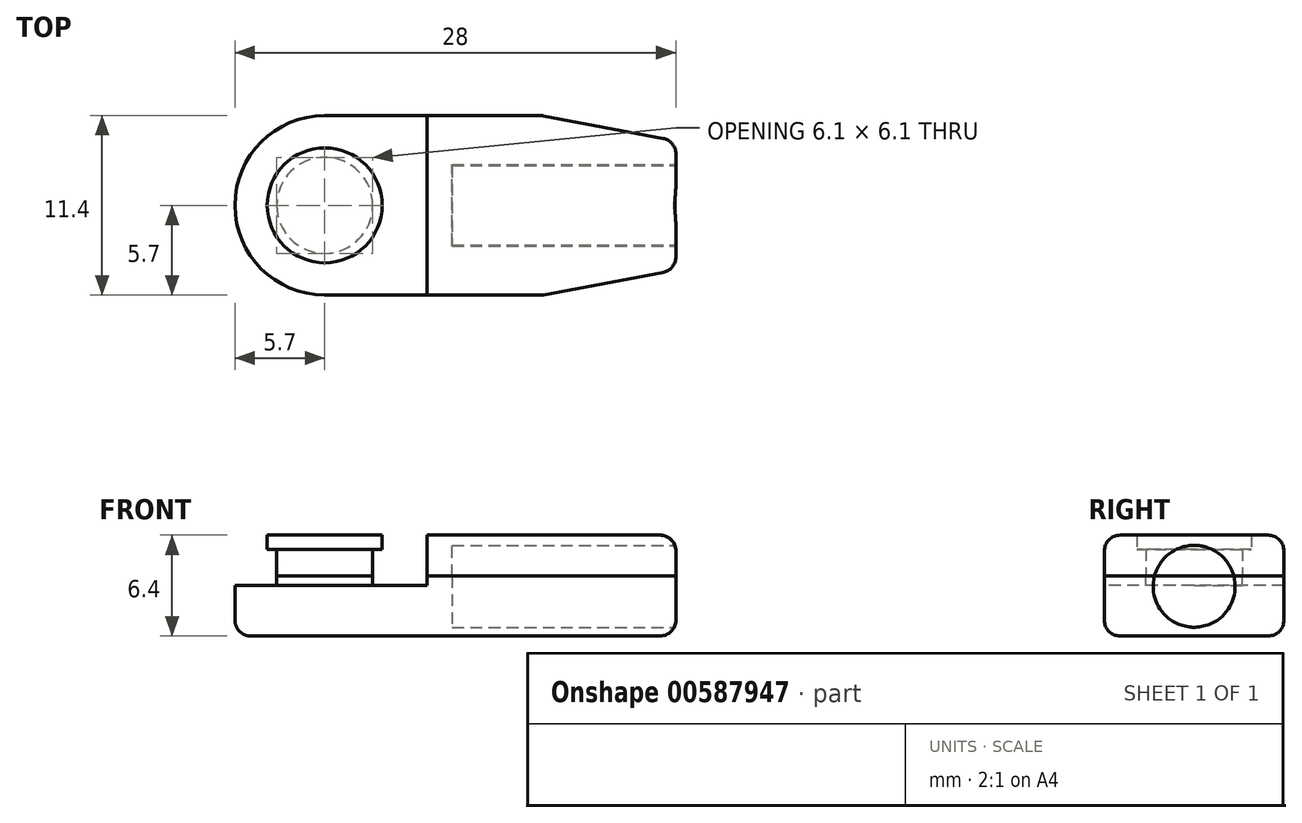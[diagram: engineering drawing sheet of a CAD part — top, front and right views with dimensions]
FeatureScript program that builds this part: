
annotation { "Feature Type Name" : "Feature", "Feature Type Description" : "" }
export const myFeature = defineFeature(function(context is Context, id is Id, definition is map)
    precondition{}
    {
        {
            var Q0;
            Q0=qCreatedBy(makeId("Top.planeOp"),FACE);
            var sketch = newSketch(context, id + "F0", { "sketchPlane" : qUnion([Q0])});
            skLineSegment(sketch, "E0.bottom", {"start": v(6.5, 5.7) * mm, "end": v(13.8, 5.7) * mm});
            skLineSegment(sketch, "E0.top", {"start": v(6.5, -5.7) * mm, "end": v(13.8, -5.7) * mm});
            skLineSegment(sketch, "E0.left", {"start": v(6.5, 5.7) * mm, "end": v(6.5, -5.7) * mm});
            skLineSegment(sketch, "E1", {"start": v(22.3, 4.1) * mm, "end": v(22.3, -4.1) * mm});
            skLineSegment(sketch, "E2", {"start": v(22.3, 4.1) * mm, "end": v(13.8, 5.7) * mm});
            skLineSegment(sketch, "E3", {"start": v(13.8, -5.7) * mm, "end": v(22.3, -4.1) * mm});
            skLineSegment(sketch, "E4.bottom", {"start": v(6.5, 5.7) * mm, "end": v(0, 5.7) * mm});
            skLineSegment(sketch, "E4.top", {"start": v(6.5, -5.7) * mm, "end": v(0, -5.7) * mm});
            skArc(sketch, "E5", {"start": v(0, 5.7) * mm, "mid": v(-5.7, 0) * mm, "end": v(0, -5.7) * mm});
            skCircle(sketch, "E6", {"center": v(0, 0) * mm, "radius": 3.05 * mm});
            skCircle(sketch, "E7", {"center": v(0, 0) * mm, "radius": 3.65 * mm});
            skLineSegment(sketch, "E8", {"start": v(-5.7, 0) * mm, "end": v(22.3, 0) * mm});
            skSolve(sketch);
        }
        {
            var Q0;
            Q0=makeQuery(id+"F0.imprint","IMPRINT",FACE,{"disambiguationData":[TD([[makeQuery(id+"F0.imprint","IMPRINT",EDGE,{"derivedFrom":sQuery(id+"F0.wireOp",EDGE,"E6")}),1.0]])]});
            extrude(context, id + "F1", {"entities" : qUnion([Q0]), "depth" : 1.7 * mm, "offsetDistance" : 25 * mm});
        }
        {
            var Q0;
            Q0=makeQuery(id+"F0.imprint","IMPRINT",FACE,{"disambiguationData":[TD([[makeQuery(id+"F0.imprint","IMPRINT",EDGE,{"derivedFrom":sQuery(id+"F0.wireOp",EDGE,"E0.bottom")}),-1.0]])]});
            var Q1;
            {var subQ1=sQuery(id+"F0.wireOp",EDGE,"E0.top");Q1=makeQuery(id+"F0.imprint","IMPRINT",FACE,{"disambiguationData":[TD([[makeQuery(id+"F0.imprint","IMPRINT",EDGE,{"derivedFrom":subQ1}),1.0]])]});}
            extrude(context, id + "F2", {"entities" : qUnion([Q0, Q1]), "depth" : 2.6 * mm, "offsetDistance" : 25 * mm});
        }
        {
            var Q0;
            Q0=makeQuery(id+"F0.imprint","IMPRINT",FACE,{"disambiguationData":[TD([[makeQuery(id+"F0.imprint","IMPRINT",EDGE,{"derivedFrom":sQuery(id+"F0.wireOp",EDGE,"E4.bottom")}),1.0]])]});
            var Q1;
            Q1=makeQuery(id+"F0.imprint","IMPRINT",FACE,{"disambiguationData":[TD([[makeQuery(id+"F0.imprint","IMPRINT",EDGE,{"derivedFrom":sQuery(id+"F0.wireOp",EDGE,"E0.bottom")}),-1.0]])]});
            var Q2;
            Q2=makeQuery(id+"F0.imprint","IMPRINT",FACE,{"disambiguationData":[TD([[makeQuery(id+"F0.imprint","IMPRINT",EDGE,{"derivedFrom":sQuery(id+"F0.wireOp",EDGE,"E6")}),-1.0]])]});
            var Q3;
            Q3=makeQuery(id+"F0.imprint","IMPRINT",FACE,{"disambiguationData":[TD([[makeQuery(id+"F0.imprint","IMPRINT",EDGE,{"derivedFrom":sQuery(id+"F0.wireOp",EDGE,"E6")}),1.0]])]});
            var Q4;
            {var subQ5=sQuery(id+"F0.wireOp",EDGE,"E4.top");Q4=makeQuery(id+"F0.imprint","IMPRINT",FACE,{"disambiguationData":[TD([[makeQuery(id+"F0.imprint","IMPRINT",EDGE,{"derivedFrom":subQ5}),-1.0]])]});}
            var Q5;
            {var subQ1=sQuery(id+"F0.wireOp",EDGE,"E0.top");Q5=makeQuery(id+"F0.imprint","IMPRINT",FACE,{"disambiguationData":[TD([[makeQuery(id+"F0.imprint","IMPRINT",EDGE,{"derivedFrom":subQ1}),1.0]])]});}
            extrude(context, id + "F3", {"entities" : qUnion([Q0, Q1, Q2, Q3, Q4, Q5]), "depth" : -3.8 * mm, "offsetDistance" : 25 * mm});
        }
        {
            var Q0;
            Q0=makeQuery(id+"F2.opExtrude","SWEPT_FACE",FACE,{"disambiguationData":[OSD([sQuery(id+"F0.wireOp",EDGE,"E1")])]});
            var sketch = newSketch(context, id + "F4", { "sketchPlane" : qUnion([Q0])});
            skCircle(sketch, "E9", {"center": v(0, -0.65) * mm, "radius": 2.6 * mm});
            skSolve(sketch);
        }
        {
            var Q0;
            {var subQ0=sQuery(id+"F4.wireOp",EDGE,"E9");var subQ1=makeQuery(id+"F2.opExtrude","CAP_EDGE",EDGE,{"disambiguationData":[OSD([sQuery(id+"F0.wireOp",EDGE,"E1")])],"isStart":true});var subQ2=makeQuery(id+"F4.imprint","INTERSECT",VERTEX,{"disambiguationData":[OD(0.0)],"derivedFrom":[subQ1,subQ0]});Q0=makeQuery(id+"F4.imprint","IMPRINT",FACE,{"disambiguationData":[TD([[makeQuery(id+"F4.imprint","IMPRINT",EDGE,{"disambiguationData":[TD([[subQ2,-1.0]])],"derivedFrom":subQ0}),1.0]])]});}
            var Q1;
            {var subQ0=sQuery(id+"F4.wireOp",EDGE,"E9");var subQ1=makeQuery(id+"F2.opExtrude","CAP_EDGE",EDGE,{"disambiguationData":[OSD([sQuery(id+"F0.wireOp",EDGE,"E1")])],"isStart":true});var subQ2=makeQuery(id+"F4.imprint","INTERSECT",VERTEX,{"disambiguationData":[OD(0.0)],"derivedFrom":[subQ1,subQ0]});Q1=makeQuery(id+"F4.imprint","IMPRINT",FACE,{"disambiguationData":[TD([[makeQuery(id+"F4.imprint","IMPRINT",EDGE,{"disambiguationData":[TD([[subQ2,1.0]])],"derivedFrom":subQ0}),1.0]])]});}
            var Q2;
            Q2=sQuery(id+"F4.wireOp",EDGE,"E9");
            extrude(context, id + "F5", {"entities" : qUnion([Q0, Q1]), "operationType" : NewBodyOperationType.REMOVE, "surfaceEntities" : qUnion([Q2]), "oppositeDirection" : true, "depth" : 14.2 * mm, "offsetDistance" : 25 * mm});
        }
        {
            var Q0;
            Q0=makeQuery(id+"F1.opExtrude","CAP_FACE",FACE,{"disambiguationData":[OSD([sQuery(id+"F0.wireOp",EDGE,"E6")])],"isStart":false});
            var sketch = newSketch(context, id + "F6", { "sketchPlane" : qUnion([Q0])});
            skCircle(sketch, "E10.0", {"center": v(0, 0) * mm, "radius": 3.65 * mm});
            skSolve(sketch);
        }
        {
            var Q0;
            Q0 = qSketchRegion(id + "F6", true);
            extrude(context, id + "F7", {"entities" : qUnion([Q0]), "operationType" : NewBodyOperationType.ADD, "depth" : 0.9 * mm, "offsetDistance" : 25 * mm});
        }
        {
            var Q0;
            Q0=makeQuery(id+"F0.imprint","IMPRINT",FACE,{"disambiguationData":[TD([[makeQuery(id+"F0.imprint","IMPRINT",EDGE,{"derivedFrom":sQuery(id+"F0.wireOp",EDGE,"E4.bottom")}),1.0]])]});
            var Q1;
            Q1=makeQuery(id+"F0.imprint","IMPRINT",FACE,{"disambiguationData":[TD([[makeQuery(id+"F0.imprint","IMPRINT",EDGE,{"derivedFrom":sQuery(id+"F0.wireOp",EDGE,"E6")}),-1.0]])]});
            var Q2;
            {var subQ5=sQuery(id+"F0.wireOp",EDGE,"E4.top");Q2=makeQuery(id+"F0.imprint","IMPRINT",FACE,{"disambiguationData":[TD([[makeQuery(id+"F0.imprint","IMPRINT",EDGE,{"derivedFrom":subQ5}),-1.0]])]});}
            extrude(context, id + "F8", {"entities" : qUnion([Q0, Q1, Q2]), "operationType" : NewBodyOperationType.REMOVE, "oppositeDirection" : true, "depth" : 0.6 * mm, "offsetDistance" : 25 * mm});
        }
        {
            var Q0;
            Q0=makeQuery(id+"F2.opExtrude","CAP_EDGE",EDGE,{"disambiguationData":[OSD([sQuery(id+"F0.wireOp",EDGE,"E0.top")])],"isStart":false});
            var Q1;
            Q1=makeQuery(id+"F2.opExtrude","CAP_EDGE",EDGE,{"disambiguationData":[OSD([sQuery(id+"F0.wireOp",EDGE,"E3")])],"isStart":false});
            var Q2;
            Q2=makeQuery(id+"F2.opExtrude","CAP_EDGE",EDGE,{"disambiguationData":[OSD([sQuery(id+"F0.wireOp",EDGE,"E1")])],"isStart":false});
            var Q3;
            Q3=makeQuery(id+"F2.opExtrude","CAP_EDGE",EDGE,{"disambiguationData":[OSD([sQuery(id+"F0.wireOp",EDGE,"E2")])],"isStart":false});
            var Q4;
            Q4=makeQuery(id+"F2.opExtrude","CAP_EDGE",EDGE,{"disambiguationData":[OSD([sQuery(id+"F0.wireOp",EDGE,"E0.bottom")])],"isStart":false});
            var Q5;
            Q5=makeQuery(id+"F3.opExtrude","CAP_EDGE",EDGE,{"disambiguationData":[OSD([sQuery(id+"F0.wireOp",EDGE,"E1")])],"isStart":false});
            var Q6;
            Q6=makeQuery(id+"F3.opExtrude","SWEPT_EDGE",EDGE,{"disambiguationData":[OSD([sQuery(id+"F0.wireOp",EDGE,"E1"),sQuery(id+"F0.wireOp",EDGE,"E2")])]});
            var Q7;
            Q7=makeQuery(id+"F2.opExtrude","SWEPT_EDGE",EDGE,{"disambiguationData":[OSD([sQuery(id+"F0.wireOp",EDGE,"E1"),sQuery(id+"F0.wireOp",EDGE,"E2")])]});
            var Q8;
            Q8=makeQuery(id+"F3.opExtrude","SWEPT_EDGE",EDGE,{"disambiguationData":[OSD([sQuery(id+"F0.wireOp",EDGE,"E1"),sQuery(id+"F0.wireOp",EDGE,"E3")])]});
            var Q9;
            Q9=makeQuery(id+"F2.opExtrude","SWEPT_EDGE",EDGE,{"disambiguationData":[OSD([sQuery(id+"F0.wireOp",EDGE,"E1"),sQuery(id+"F0.wireOp",EDGE,"E3")])]});
            var Q10;
            Q10=makeQuery(id+"F3.opExtrude","CAP_EDGE",EDGE,{"disambiguationData":[OSD([sQuery(id+"F0.wireOp",EDGE,"E3")])],"isStart":false});
            var Q11;
            Q11=makeQuery(id+"F3.opExtrude","CAP_EDGE",EDGE,{"disambiguationData":[OSD([sQuery(id+"F0.wireOp",EDGE,"E0.top"),sQuery(id+"F0.wireOp",EDGE,"E4.top")])],"isStart":false});
            var Q12;
            Q12=makeQuery(id+"F3.opExtrude","CAP_EDGE",EDGE,{"disambiguationData":[OSD([sQuery(id+"F0.wireOp",EDGE,"E5")])],"isStart":false});
            var Q13;
            Q13=makeQuery(id+"F3.opExtrude","CAP_EDGE",EDGE,{"disambiguationData":[OSD([sQuery(id+"F0.wireOp",EDGE,"E0.bottom"),sQuery(id+"F0.wireOp",EDGE,"E4.bottom")])],"isStart":false});
            var Q14;
            Q14=makeQuery(id+"F3.opExtrude","CAP_EDGE",EDGE,{"disambiguationData":[OSD([sQuery(id+"F0.wireOp",EDGE,"E2")])],"isStart":false});
            var Q15;
            Q15=makeQuery(id+"F2.opExtrude","SWEPT_EDGE",EDGE,{"disambiguationData":[OSD([sQuery(id+"F0.wireOp",EDGE,"E0.top"),sQuery(id+"F0.wireOp",EDGE,"E3")])]});
            var Q16;
            Q16=makeQuery(id+"F3.opExtrude","SWEPT_EDGE",EDGE,{"disambiguationData":[OSD([sQuery(id+"F0.wireOp",EDGE,"E0.top"),sQuery(id+"F0.wireOp",EDGE,"E3")])]});
            var Q17;
            Q17=makeQuery(id+"F3.opExtrude","SWEPT_EDGE",EDGE,{"disambiguationData":[OSD([sQuery(id+"F0.wireOp",EDGE,"E0.bottom"),sQuery(id+"F0.wireOp",EDGE,"E2")])]});
            var Q18;
            Q18=makeQuery(id+"F2.opExtrude","SWEPT_EDGE",EDGE,{"disambiguationData":[OSD([sQuery(id+"F0.wireOp",EDGE,"E0.bottom"),sQuery(id+"F0.wireOp",EDGE,"E2")])]});
            fillet(context, id + "F9", {"entities" : qUnion([Q0, Q1, Q2, Q3, Q4, Q5, Q6, Q7, Q8, Q9, Q10, Q11, Q12, Q13, Q14, Q15, Q16, Q17, Q18]), "radius" : 1 * mm, "tangentPropagation" : true, "allowEdgeOverflow" : false});
        }
    });
